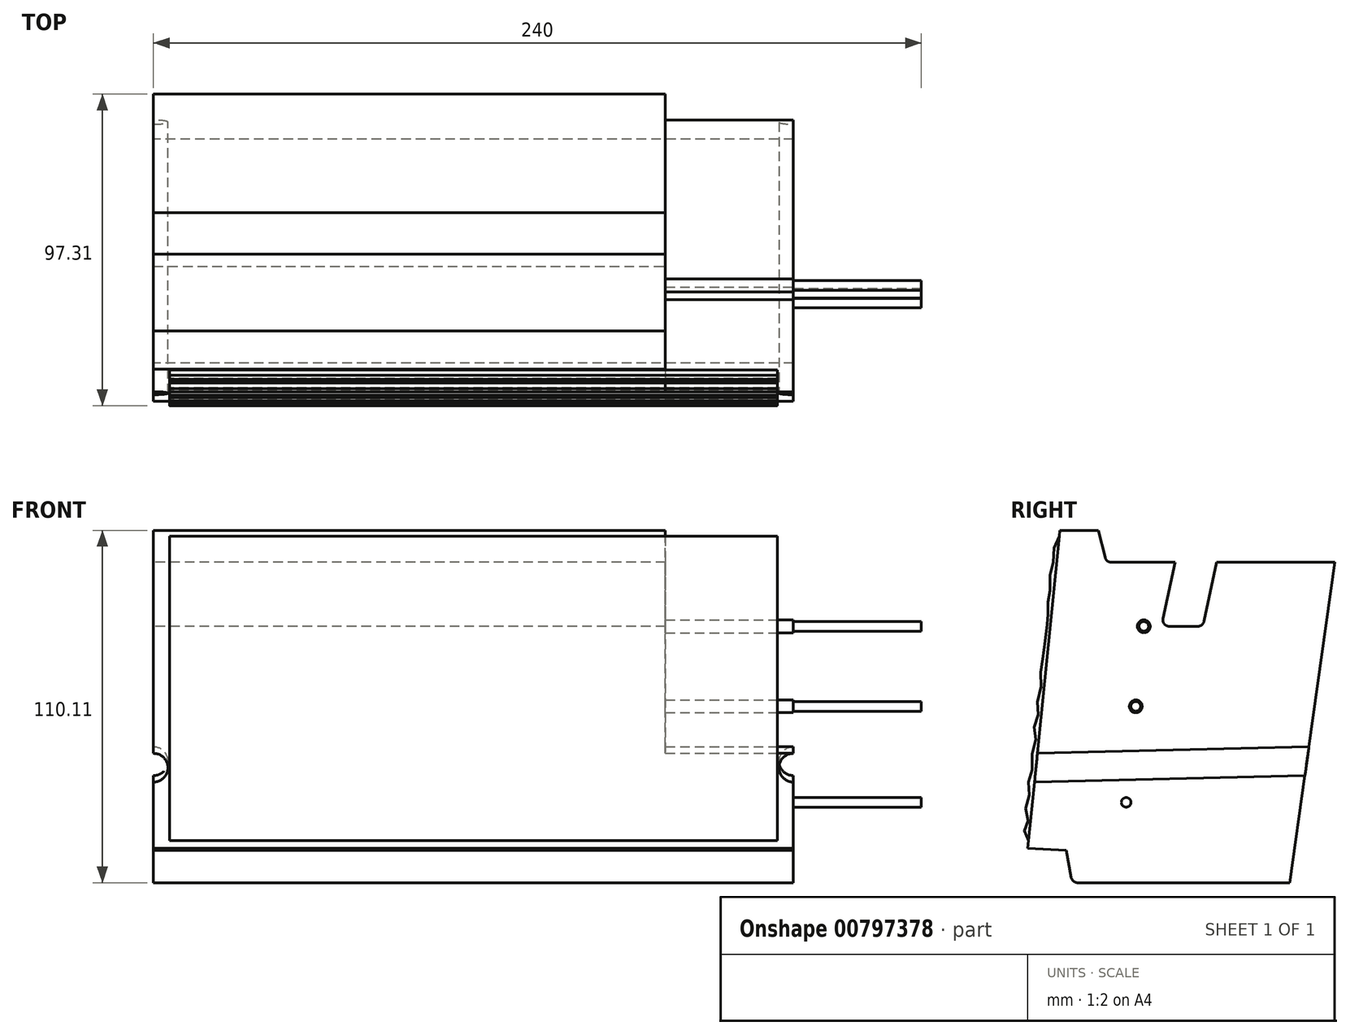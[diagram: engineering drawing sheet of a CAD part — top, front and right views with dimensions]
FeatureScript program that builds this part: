
annotation { "Feature Type Name" : "Feature", "Feature Type Description" : "" }
export const myFeature = defineFeature(function(context is Context, id is Id, definition is map)
    precondition{}
    {
        {
            var Q0;
            Q0=qCreatedBy(makeId("Right.planeOp"),FACE);
            var sketch = newSketch(context, id + "F0", { "sketchPlane" : qUnion([Q0])});
            skLineSegment(sketch, "E0", {"start": v(0, 0) * mm, "end": v(68, 0) * mm});
            skLineSegment(sketch, "E1", {"start": v(68, 0) * mm, "end": v(82.12, 100.1) * mm});
            skLineSegment(sketch, "E2", {"start": v(82.12, 100.1) * mm, "end": v(45.12, 100.1) * mm});
            skLineSegment(sketch, "E3", {"start": v(45.12, 100.1) * mm, "end": v(40.84, 80.1) * mm});
            skLineSegment(sketch, "E4", {"start": v(40.84, 80.1) * mm, "end": v(27.84, 80.1) * mm});
            skLineSegment(sketch, "E5", {"start": v(27.84, 80.1) * mm, "end": v(32.12, 100.1) * mm});
            skLineSegment(sketch, "E6", {"start": v(32.12, 100.1) * mm, "end": v(10.63, 100.1) * mm});
            skLineSegment(sketch, "E7", {"start": v(10.63, 100.1) * mm, "end": v(8.12, 110.1) * mm});
            skLineSegment(sketch, "E8", {"start": v(8.12, 110.1) * mm, "end": v(-3.88, 110.1) * mm});
            skLineSegment(sketch, "E9", {"start": v(-3.88, 110.1) * mm, "end": v(-13.88, 10.7) * mm});
            skLineSegment(sketch, "E10", {"start": v(-13.88, 10.7) * mm, "end": v(-1.88, 10.1) * mm});
            skLineSegment(sketch, "E11", {"start": v(-1.88, 10.1) * mm, "end": v(0, 0) * mm});
            skSolve(sketch);
        }
        {
            var Q0;
            Q0 = qSketchRegion(id + "F0", true);
            extrude(context, id + "F1", {"entities" : qUnion([Q0]), "depth" : 200 * mm, "offsetDistance" : 25 * mm});
        }
        {
            var Q0;
            Q0=makeQuery(id+"F1.opExtrude","SWEPT_EDGE",EDGE,{"disambiguationData":[OSD([sQuery(id+"F0.wireOp",EDGE,"E6"),sQuery(id+"F0.wireOp",EDGE,"E7")])]});
            var Q1;
            Q1=makeQuery(id+"F1.opExtrude","SWEPT_EDGE",EDGE,{"disambiguationData":[OSD([sQuery(id+"F0.wireOp",EDGE,"E4"),sQuery(id+"F0.wireOp",EDGE,"E5")])]});
            var Q2;
            Q2=makeQuery(id+"F1.opExtrude","SWEPT_EDGE",EDGE,{"disambiguationData":[OSD([sQuery(id+"F0.wireOp",EDGE,"E3"),sQuery(id+"F0.wireOp",EDGE,"E4")])]});
            var Q3;
            Q3=makeQuery(id+"F1.opExtrude","SWEPT_EDGE",EDGE,{"disambiguationData":[OSD([sQuery(id+"F0.wireOp",EDGE,"E0"),sQuery(id+"F0.wireOp",EDGE,"E11")])]});
            fillet(context, id + "F2", {"entities" : qUnion([Q0, Q1, Q2, Q3]), "radius" : 2 * mm, "tangentPropagation" : true, "allowEdgeOverflow" : false});
        }
        {
            var Q0;
            Q0=makeQuery(id+"F1.opExtrude","CAP_FACE",FACE,{"disambiguationData":[OSD([sQuery(id+"F0.wireOp",EDGE,"E0"),sQuery(id+"F0.wireOp",EDGE,"E1"),sQuery(id+"F0.wireOp",EDGE,"E2"),sQuery(id+"F0.wireOp",EDGE,"E3"),sQuery(id+"F0.wireOp",EDGE,"E4"),sQuery(id+"F0.wireOp",EDGE,"E5"),sQuery(id+"F0.wireOp",EDGE,"E6"),sQuery(id+"F0.wireOp",EDGE,"E7"),sQuery(id+"F0.wireOp",EDGE,"E8"),sQuery(id+"F0.wireOp",EDGE,"E9"),sQuery(id+"F0.wireOp",EDGE,"E10"),sQuery(id+"F0.wireOp",EDGE,"E11")])],"isStart":false});
            var sketch = newSketch(context, id + "F3", { "sketchPlane" : qUnion([Q0])});
            skLineSegment(sketch, "E12", {"start": v(-11.34, 35.93) * mm, "end": v(89.67, 38.34) * mm});
            skSolve(sketch);
        }
        {
            var Q0;
            Q0=makeQuery(id+"F1.opExtrude","SWEPT_FACE",FACE,{"disambiguationData":[OSD([sQuery(id+"F0.wireOp",EDGE,"E9")])]});
            var sketch = newSketch(context, id + "F4", { "sketchPlane" : qUnion([Q0])});
            skLineSegment(sketch, "E13.0", {"start": v(200, 34.62) * mm, "end": v(200, 47.13) * mm});
            skCircle(sketch, "E14", {"center": v(200, 34.62) * mm, "radius": 4.5 * mm});
            skSolve(sketch);
        }
        {
            var Q0;
            {var subQ0=sQuery(id+"F4.wireOp",EDGE,"E13.0");var subQ1=makeQuery(id+"F1.opExtrude","CAP_EDGE",EDGE,{"disambiguationData":[OSD([sQuery(id+"F0.wireOp",EDGE,"E9")])],"isStart":false});var subQ2=makeQuery(id+"F4.imprint","INTERSECT",VERTEX,{"disambiguationData":[OD(1.0)],"derivedFrom":[subQ1,subQ0]});Q0=makeQuery(id+"F4.imprint","IMPRINT",FACE,{"disambiguationData":[TD([[makeQuery(id+"F4.imprint","IMPRINT",EDGE,{"disambiguationData":[TD([[subQ2,1.0]])],"derivedFrom":subQ0}),-1.0]])]});}
            var Q1;
            Q1=sQuery(id+"F3.wireOp",EDGE,"E12");
            sweep(context, id + "F5", {"profiles" : qUnion([Q0]), "path" : qUnion([Q1])});
        }
        {
            var Q0;
            Q0=makeQuery(id+"F1.opExtrude","CAP_FACE",FACE,{"disambiguationData":[OSD([sQuery(id+"F0.wireOp",EDGE,"E0"),sQuery(id+"F0.wireOp",EDGE,"E1"),sQuery(id+"F0.wireOp",EDGE,"E2"),sQuery(id+"F0.wireOp",EDGE,"E3"),sQuery(id+"F0.wireOp",EDGE,"E4"),sQuery(id+"F0.wireOp",EDGE,"E5"),sQuery(id+"F0.wireOp",EDGE,"E6"),sQuery(id+"F0.wireOp",EDGE,"E7"),sQuery(id+"F0.wireOp",EDGE,"E8"),sQuery(id+"F0.wireOp",EDGE,"E9"),sQuery(id+"F0.wireOp",EDGE,"E10"),sQuery(id+"F0.wireOp",EDGE,"E11")])],"isStart":true});
            var Q1;
            {var subQ0=sQuery(id+"F0.wireOp",EDGE,"E9");var subQ1=sQuery(id+"F0.wireOp",EDGE,"E5");var subQ2=sQuery(id+"F0.wireOp",EDGE,"E4");var subQ3=sQuery(id+"F0.wireOp",EDGE,"E8");var subQ4=sQuery(id+"F0.wireOp",EDGE,"E3");var subQ5=sQuery(id+"F0.wireOp",EDGE,"E7");var subQ6=sQuery(id+"F0.wireOp",EDGE,"E6");var subQ7=sQuery(id+"F0.wireOp",EDGE,"E1");var subQ8=sQuery(id+"F0.wireOp",EDGE,"E2");Q1=makeQuery(id+"F5.boolean.opBoolean","SPLIT",FACE,{"disambiguationData":[TD([makeQuery(id+"F1.opExtrude","SWEPT_FACE",FACE,{"disambiguationData":[OSD([subQ8])]})])],"derivedFrom":makeQuery(id+"F1.opExtrude","CAP_FACE",FACE,{"disambiguationData":[OSD([sQuery(id+"F0.wireOp",EDGE,"E0"),subQ7,subQ8,subQ4,subQ2,subQ1,subQ6,subQ5,subQ3,subQ0,sQuery(id+"F0.wireOp",EDGE,"E10"),sQuery(id+"F0.wireOp",EDGE,"E11")])],"isStart":false})});}
            cPlane(context, id + "F6", {"entities" : qUnion([Q0, Q1]), "cplaneType" : CPlaneType.MID_PLANE, "offset" : 25 * mm, "width" : 150 * mm, "height" : 150 * mm});
        }
        {
            var Q0;
            Q0=makeQuery(id+"F5.opSweep","SWEPT_BODY",BODY,{"disambiguationData":[OSD([sQuery(id+"F0.wireOp",EDGE,"E9"),sQuery(id+"F3.wireOp",EDGE,"E12"),sQuery(id+"F4.wireOp",EDGE,"E13.0"),sQuery(id+"F4.wireOp",EDGE,"E14")])]});
            var Q1;
            Q1=qCreatedBy(id+"F6.planeOp",FACE);
            mirror(context, id + "F7", {"operationType" : NewBodyOperationType.REMOVE, "entities" : qUnion([Q0]), "mirrorPlane" : qUnion([Q1])});
        }
        {
            var Q0;
            Q0=makeQuery(id+"F5.opSweep","SWEPT_BODY",BODY,{"disambiguationData":[OSD([sQuery(id+"F0.wireOp",EDGE,"E9"),sQuery(id+"F3.wireOp",EDGE,"E12"),sQuery(id+"F4.wireOp",EDGE,"E13.0"),sQuery(id+"F4.wireOp",EDGE,"E14")])]});
            var Q1;
            Q1=makeQuery(id+"F1.opExtrude","SWEPT_BODY",BODY,{"disambiguationData":[OSD([sQuery(id+"F0.wireOp",EDGE,"E0"),sQuery(id+"F0.wireOp",EDGE,"E1"),sQuery(id+"F0.wireOp",EDGE,"E2"),sQuery(id+"F0.wireOp",EDGE,"E3"),sQuery(id+"F0.wireOp",EDGE,"E4"),sQuery(id+"F0.wireOp",EDGE,"E5"),sQuery(id+"F0.wireOp",EDGE,"E6"),sQuery(id+"F0.wireOp",EDGE,"E7"),sQuery(id+"F0.wireOp",EDGE,"E8"),sQuery(id+"F0.wireOp",EDGE,"E9"),sQuery(id+"F0.wireOp",EDGE,"E10"),sQuery(id+"F0.wireOp",EDGE,"E11")])]});
            booleanBodies(context, id + "F8", {"operationType" : BooleanOperationType.SUBTRACTION, "tools" : qUnion([Q0]), "targets" : qUnion([Q1])});
        }
        {
            var Q0;
            {var subQ0=sQuery(id+"F0.wireOp",EDGE,"E9");var subQ1=sQuery(id+"F0.wireOp",EDGE,"E5");var subQ2=sQuery(id+"F0.wireOp",EDGE,"E4");var subQ3=sQuery(id+"F0.wireOp",EDGE,"E8");var subQ4=sQuery(id+"F0.wireOp",EDGE,"E3");var subQ5=sQuery(id+"F0.wireOp",EDGE,"E7");var subQ6=sQuery(id+"F0.wireOp",EDGE,"E6");var subQ7=sQuery(id+"F0.wireOp",EDGE,"E1");var subQ8=sQuery(id+"F0.wireOp",EDGE,"E2");Q0=makeQuery(id+"F8.opBoolean","SPLIT",FACE,{"disambiguationData":[TD([makeQuery(id+"F1.opExtrude","SWEPT_FACE",FACE,{"disambiguationData":[OSD([subQ8])]})])],"derivedFrom":makeQuery(id+"F1.opExtrude","CAP_FACE",FACE,{"disambiguationData":[OSD([sQuery(id+"F0.wireOp",EDGE,"E0"),subQ7,subQ8,subQ4,subQ2,subQ1,subQ6,subQ5,subQ3,subQ0,sQuery(id+"F0.wireOp",EDGE,"E10"),sQuery(id+"F0.wireOp",EDGE,"E11")])],"isStart":false})});}
            cPlane(context, id + "F9", {"entities" : qUnion([Q0]), "cplaneType" : CPlaneType.OFFSET, "offset" : 5 * mm, "oppositeDirection" : true, "width" : 150 * mm, "height" : 150 * mm});
        }
        {
            var Q0;
            Q0=qCreatedBy(id+"F9.planeOp",FACE);
            var sketch = newSketch(context, id + "F10", { "sketchPlane" : qUnion([Q0])});
            skFitSpline(sketch, "E15", {"points": [v(-4.07, 108.22) * mm, v(-5.7, 105.52) * mm, v(-5.69, 104.27) * mm, v(-5.82, 100.86) * mm, v(-6.65, 98.2) * mm, v(-6.96, 95.64) * mm, v(-6.76, 92.01) * mm, v(-7.55, 89.48) * mm, v(-7.56, 87.88) * mm, v(-7.96, 85.6) * mm, v(-7.55, 83.57) * mm, v(-8.11, 81.77) * mm, v(-7.78, 80.25) * mm, v(-8.43, 76.1) * mm, v(-9.03, 70.81) * mm, v(-9.75, 68.08) * mm, v(-9.88, 65.4) * mm, v(-9.7, 63.32) * mm, v(-10.29, 58.24) * mm, v(-10.9, 56.09) * mm, v(-10.64, 53.21) * mm, v(-10.9, 52.07) * mm, v(-11.98, 49.13) * mm, v(-10.96, 46.6) * mm, v(-11.5, 44.38) * mm, v(-12.45, 41.3) * mm, v(-12.63, 37.63) * mm, v(-12.71, 34.27) * mm, v(-13.65, 32.06) * mm, v(-13.52, 29.52) * mm, v(-13.45, 27.18) * mm, v(-14.17, 24.78) * mm, v(-14.52, 21.82) * mm, v(-13.79, 19.82) * mm, v(-14.66, 17.74) * mm, v(-14.92, 16.6) * mm, v(-15.12, 14.53) * mm, v(-13.63, 13.18) * mm], "startDerivative": vector(-121.63, -96) * mm, "endDerivative": vector(79.77, -48.28) * mm});
            skLineSegment(sketch, "E16.0", {"start": v(-11.8, 31.45) * mm, "end": v(-13.88, 10.7) * mm});
            skLineSegment(sketch, "E17.0", {"start": v(-3.88, 110.1) * mm, "end": v(-10.9, 40.4) * mm});
            skLineSegment(sketch, "E18", {"start": v(-10.9, 40.4) * mm, "end": v(-11.8, 31.45) * mm});
            skSolve(sketch);
        }
        {
            var Q0;
            Q0 = qSketchRegion(id + "F10", true);
            extrude(context, id + "F11", {"entities" : qUnion([Q0]), "operationType" : NewBodyOperationType.ADD, "oppositeDirection" : true, "depth" : 190 * mm, "offsetDistance" : 25 * mm});
        }
        {
            var Q0;
            {var subQ0=sQuery(id+"F0.wireOp",EDGE,"E9");var subQ1=sQuery(id+"F0.wireOp",EDGE,"E5");var subQ2=sQuery(id+"F0.wireOp",EDGE,"E4");var subQ3=sQuery(id+"F0.wireOp",EDGE,"E8");var subQ4=sQuery(id+"F0.wireOp",EDGE,"E3");var subQ5=sQuery(id+"F0.wireOp",EDGE,"E7");var subQ6=sQuery(id+"F0.wireOp",EDGE,"E6");var subQ7=sQuery(id+"F0.wireOp",EDGE,"E1");var subQ8=sQuery(id+"F0.wireOp",EDGE,"E2");Q0=makeQuery(id+"F8.opBoolean","SPLIT",FACE,{"disambiguationData":[TD([makeQuery(id+"F1.opExtrude","SWEPT_FACE",FACE,{"disambiguationData":[OSD([subQ8])]})])],"derivedFrom":makeQuery(id+"F1.opExtrude","CAP_FACE",FACE,{"disambiguationData":[OSD([sQuery(id+"F0.wireOp",EDGE,"E0"),subQ7,subQ8,subQ4,subQ2,subQ1,subQ6,subQ5,subQ3,subQ0,sQuery(id+"F0.wireOp",EDGE,"E10"),sQuery(id+"F0.wireOp",EDGE,"E11")])],"isStart":false})});}
            var sketch = newSketch(context, id + "F12", { "sketchPlane" : qUnion([Q0])});
            skLineSegment(sketch, "E19", {"start": v(24.37, 100.1) * mm, "end": v(14.3, 0) * mm});
            skCircle(sketch, "E20", {"center": v(22.36, 80.1) * mm, "radius": 2 * mm});
            skCircle(sketch, "E21", {"center": v(16.83, 25.1) * mm, "radius": 2 * mm});
            skCircle(sketch, "E22", {"center": v(19.84, 55.1) * mm, "radius": 2 * mm});
            skSolve(sketch);
        }
        {
            var Q0;
            {var subQ0=sQuery(id+"F12.wireOp",EDGE,"E20");var subQ1=sQuery(id+"F12.wireOp",EDGE,"E19");var subQ2=makeQuery(id+"F12.imprint","INTERSECT",VERTEX,{"disambiguationData":[OD(0.0)],"derivedFrom":[subQ1,subQ0]});Q0=makeQuery(id+"F12.imprint","IMPRINT",FACE,{"disambiguationData":[TD([[makeQuery(id+"F12.imprint","IMPRINT",EDGE,{"disambiguationData":[TD([[subQ2,-1.0]])],"derivedFrom":subQ1}),-1.0]])]});}
            var Q1;
            {var subQ0=sQuery(id+"F12.wireOp",EDGE,"E20");var subQ1=sQuery(id+"F12.wireOp",EDGE,"E19");var subQ2=makeQuery(id+"F12.imprint","INTERSECT",VERTEX,{"disambiguationData":[OD(0.0)],"derivedFrom":[subQ1,subQ0]});Q1=makeQuery(id+"F12.imprint","IMPRINT",FACE,{"disambiguationData":[TD([[makeQuery(id+"F12.imprint","IMPRINT",EDGE,{"disambiguationData":[TD([[subQ2,-1.0]])],"derivedFrom":subQ1}),1.0]])]});}
            var Q2;
            {var subQ0=sQuery(id+"F12.wireOp",EDGE,"E22");var subQ1=sQuery(id+"F12.wireOp",EDGE,"E19");var subQ2=makeQuery(id+"F12.imprint","INTERSECT",VERTEX,{"disambiguationData":[OD(0.0)],"derivedFrom":[subQ1,subQ0]});Q2=makeQuery(id+"F12.imprint","IMPRINT",FACE,{"disambiguationData":[TD([[makeQuery(id+"F12.imprint","IMPRINT",EDGE,{"disambiguationData":[TD([[subQ2,-1.0]])],"derivedFrom":subQ1}),-1.0]])]});}
            var Q3;
            {var subQ0=sQuery(id+"F12.wireOp",EDGE,"E22");var subQ1=sQuery(id+"F12.wireOp",EDGE,"E19");var subQ2=makeQuery(id+"F12.imprint","INTERSECT",VERTEX,{"disambiguationData":[OD(0.0)],"derivedFrom":[subQ1,subQ0]});Q3=makeQuery(id+"F12.imprint","IMPRINT",FACE,{"disambiguationData":[TD([[makeQuery(id+"F12.imprint","IMPRINT",EDGE,{"disambiguationData":[TD([[subQ2,-1.0]])],"derivedFrom":subQ1}),1.0]])]});}
            var Q4;
            {var subQ0=sQuery(id+"F12.wireOp",EDGE,"E21");var subQ1=sQuery(id+"F12.wireOp",EDGE,"E19");var subQ2=makeQuery(id+"F12.imprint","INTERSECT",VERTEX,{"disambiguationData":[OD(0.0)],"derivedFrom":[subQ1,subQ0]});Q4=makeQuery(id+"F12.imprint","IMPRINT",FACE,{"disambiguationData":[TD([[makeQuery(id+"F12.imprint","IMPRINT",EDGE,{"disambiguationData":[TD([[subQ2,1.0]])],"derivedFrom":subQ1}),-1.0]])]});}
            var Q5;
            {var subQ0=sQuery(id+"F12.wireOp",EDGE,"E21");var subQ1=sQuery(id+"F12.wireOp",EDGE,"E19");var subQ2=makeQuery(id+"F12.imprint","INTERSECT",VERTEX,{"disambiguationData":[OD(0.0)],"derivedFrom":[subQ1,subQ0]});Q5=makeQuery(id+"F12.imprint","IMPRINT",FACE,{"disambiguationData":[TD([[makeQuery(id+"F12.imprint","IMPRINT",EDGE,{"disambiguationData":[TD([[subQ2,1.0]])],"derivedFrom":subQ1}),1.0]])]});}
            extrude(context, id + "F13", {"entities" : qUnion([Q0, Q1, Q2, Q3, Q4, Q5]), "operationType" : NewBodyOperationType.REMOVE, "oppositeDirection" : true, "depth" : 40 * mm, "offsetDistance" : 25 * mm});
        }
        {
            var Q0;
            Q0=makeQuery(id+"F13.boolean.opBoolean","COPY",FACE,{"derivedFrom":makeQuery(id+"F13.opExtrude","CAP_FACE",FACE,{"disambiguationData":[OSD([sQuery(id+"F12.wireOp",EDGE,"E20")])],"isStart":false})});
            var sketch = newSketch(context, id + "F14", { "sketchPlane" : qUnion([Q0])});
            skCircle(sketch, "E23", {"center": v(22.36, 80.1) * mm, "radius": 1.5 * mm});
            skCircle(sketch, "E24", {"center": v(19.84, 55.1) * mm, "radius": 1.5 * mm});
            skCircle(sketch, "E25", {"center": v(16.83, 25.1) * mm, "radius": 1.5 * mm});
            skSolve(sketch);
        }
        {
            var Q0;
            Q0=makeQuery(id+"F14.imprint","IMPRINT",FACE,{"disambiguationData":[TD([[makeQuery(id+"F14.imprint","IMPRINT",EDGE,{"derivedFrom":sQuery(id+"F14.wireOp",EDGE,"E23")}),1.0]])]});
            var Q1;
            Q1=makeQuery(id+"F14.imprint","IMPRINT",FACE,{"disambiguationData":[TD([[makeQuery(id+"F14.imprint","IMPRINT",EDGE,{"derivedFrom":sQuery(id+"F14.wireOp",EDGE,"E24")}),1.0]])]});
            var Q2;
            Q2=makeQuery(id+"F14.imprint","IMPRINT",FACE,{"disambiguationData":[TD([[makeQuery(id+"F14.imprint","IMPRINT",EDGE,{"derivedFrom":sQuery(id+"F14.wireOp",EDGE,"E25")}),1.0]])]});
            extrude(context, id + "F15", {"entities" : qUnion([Q0, Q1, Q2]), "operationType" : NewBodyOperationType.ADD, "depth" : 80 * mm, "offsetDistance" : 25 * mm});
        }
    });
